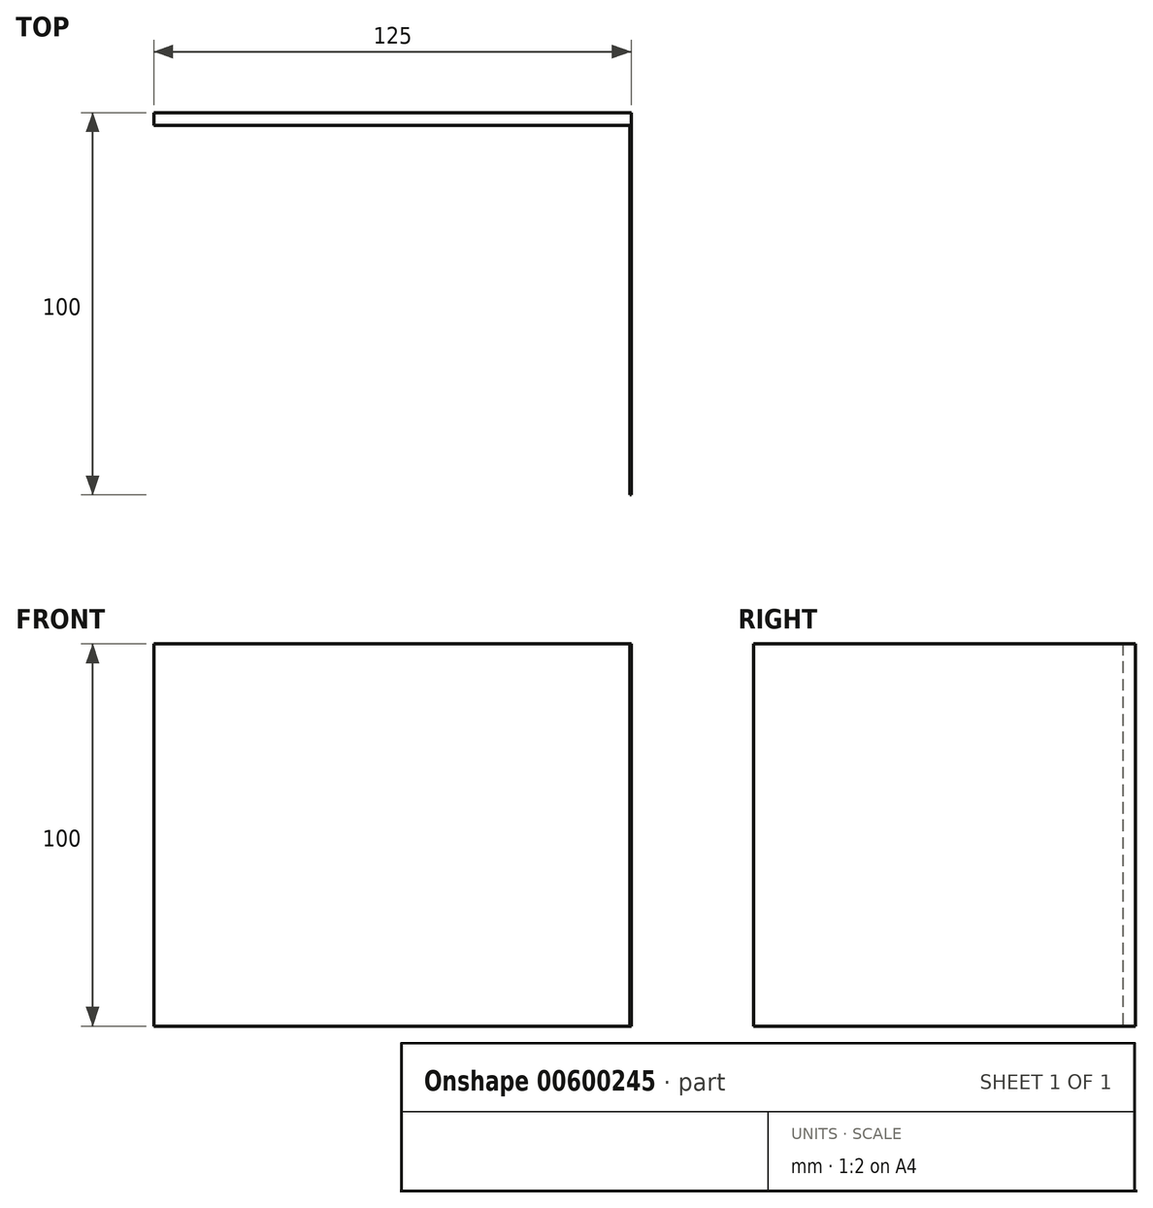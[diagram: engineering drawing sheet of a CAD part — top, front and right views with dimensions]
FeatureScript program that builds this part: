
annotation { "Feature Type Name" : "Feature", "Feature Type Description" : "" }
export const myFeature = defineFeature(function(context is Context, id is Id, definition is map)
    precondition{}
    {
        {
            var Q0;
            Q0=qCreatedBy(makeId("Top.planeOp"),FACE);
            var sketch = newSketch(context, id + "F0", { "sketchPlane" : qUnion([Q0])});
            skLineSegment(sketch, "E0.bottom", {"start": v(-62.08, 53.32) * mm, "end": v(62.92, 53.32) * mm});
            skLineSegment(sketch, "E0.top", {"start": v(-62.08, -46.68) * mm, "end": v(62.92, -46.68) * mm});
            skLineSegment(sketch, "E0.left", {"start": v(-62.08, 53.32) * mm, "end": v(-62.08, -46.68) * mm});
            skLineSegment(sketch, "E0.right", {"start": v(62.92, 53.32) * mm, "end": v(62.92, -46.68) * mm});
            skLineSegment(sketch, "E1.bottom", {"start": v(-62.5, 50) * mm, "end": v(62.5, 50) * mm});
            skLineSegment(sketch, "E1.top", {"start": v(-62.5, -50) * mm, "end": v(62.5, -50) * mm});
            skLineSegment(sketch, "E1.left", {"start": v(-62.5, 50) * mm, "end": v(-62.5, -50) * mm});
            skLineSegment(sketch, "E1.right", {"start": v(62.5, 50) * mm, "end": v(62.5, -50) * mm});
            skSolve(sketch);
        }
        {
            var Q0;
            Q0=makeQuery(id+"F0.imprint","IMPRINT",FACE,{"disambiguationData":[TD([[makeQuery(id+"F0.imprint","IMPRINT",EDGE,{"derivedFrom":sQuery(id+"F0.wireOp",EDGE,"E0.bottom")}),-1.0]])]});
            extrude(context, id + "F1", {"entities" : qUnion([Q0]), "depth" : 100 * mm, "offsetDistance" : 25 * mm});
        }
    });
